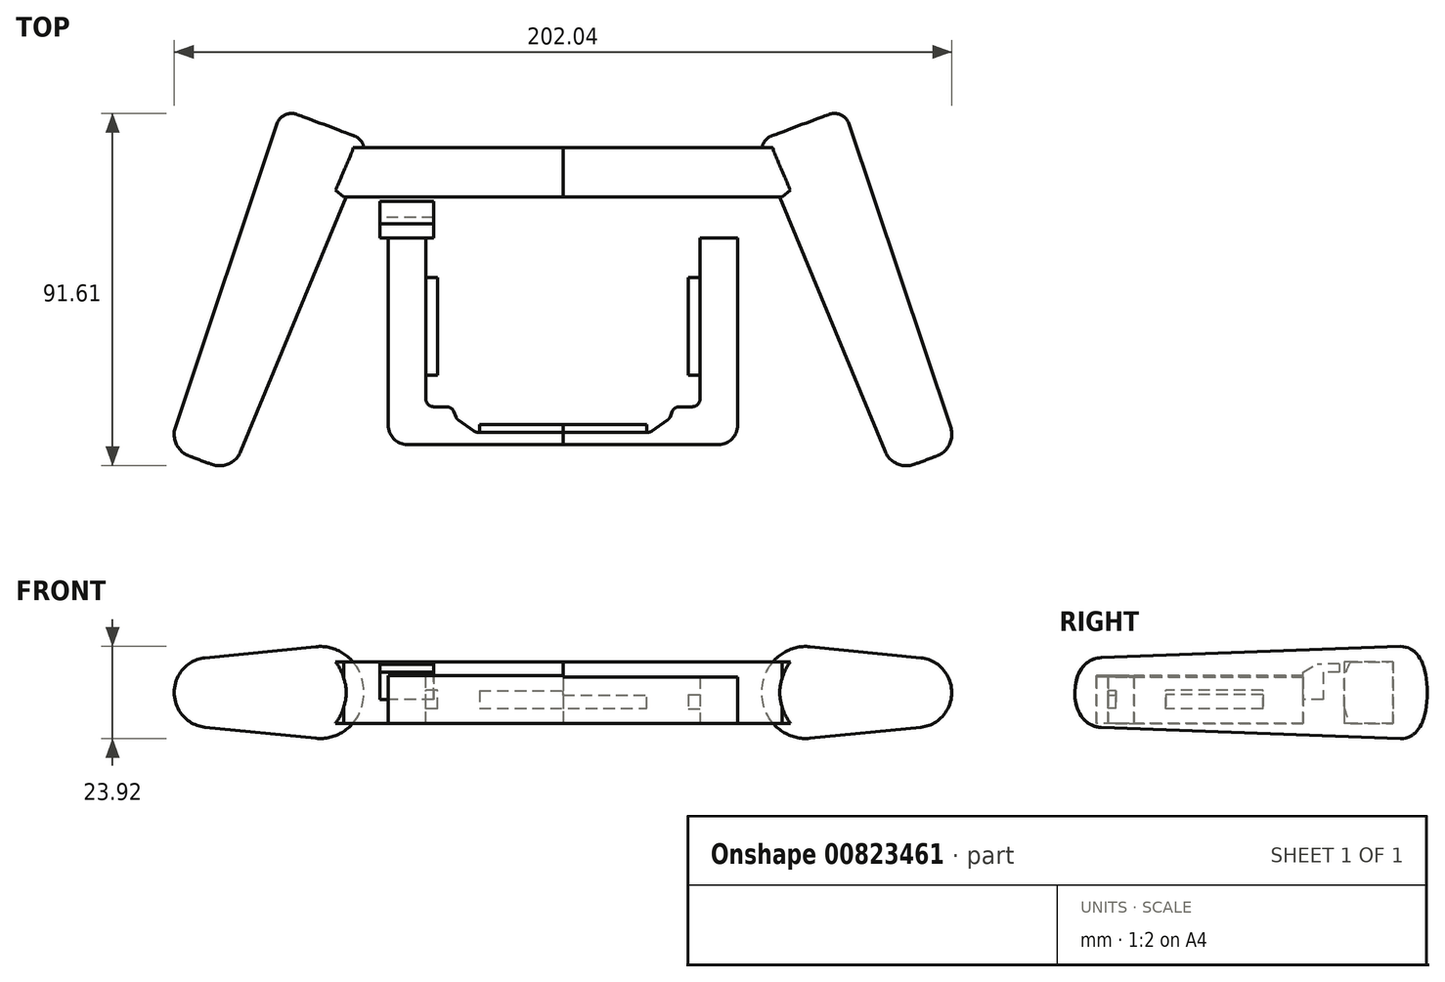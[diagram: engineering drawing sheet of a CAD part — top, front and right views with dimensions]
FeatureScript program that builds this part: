
annotation { "Feature Type Name" : "Feature", "Feature Type Description" : "" }
export const myFeature = defineFeature(function(context is Context, id is Id, definition is map)
    precondition{}
    {
        {
            var Q0;
            Q0=qCreatedBy(makeId("Top.planeOp"),FACE);
            var sketch = newSketch(context, id + "F0", { "sketchPlane" : qUnion([Q0])});
            skLineSegment(sketch, "E0", {"start": v(0, -25.8) * mm, "end": v(-45.43, -25.8) * mm});
            skLineSegment(sketch, "E1", {"start": v(-45.43, -25.8) * mm, "end": v(-45.43, 27.94) * mm});
            skLineSegment(sketch, "E2", {"start": v(-45.43, 27.94) * mm, "end": v(-35.62, 27.94) * mm});
            skLineSegment(sketch, "E3", {"start": v(-35.62, 27.94) * mm, "end": v(-35.62, -16) * mm});
            skLineSegment(sketch, "E4", {"start": v(-35.62, -16) * mm, "end": v(-28.9, -16) * mm});
            skLineSegment(sketch, "E5", {"start": v(0, -22.66) * mm, "end": v(0, -25.8) * mm});
            skLineSegment(sketch, "E6", {"start": v(-28.9, -16) * mm, "end": v(-27.58, -19.2) * mm});
            skLineSegment(sketch, "E7", {"start": v(-27.58, -19.2) * mm, "end": v(-22.63, -22.66) * mm});
            skLineSegment(sketch, "E8", {"start": v(-22.63, -22.66) * mm, "end": v(0, -22.66) * mm});
            skSolve(sketch);
        }
        {
            var Q0;
            Q0=makeQuery(id+"F0.imprint","IMPRINT",FACE,{"disambiguationData":[TD([[makeQuery(id+"F0.imprint","IMPRINT",EDGE,{"derivedFrom":sQuery(id+"F0.wireOp",EDGE,"E0")}),-1.0]])]});
            extrude(context, id + "F1", {"entities" : qUnion([Q0]), "depth" : 12 * mm, "offsetDistance" : 25 * mm});
        }
        {
            var Q0;
            Q0=makeQuery(id+"F1.opExtrude","SWEPT_FACE",FACE,{"disambiguationData":[OSD([sQuery(id+"F0.wireOp",EDGE,"E3")])]});
            var sketch = newSketch(context, id + "F2", { "sketchPlane" : qUnion([Q0])});
            skLineSegment(sketch, "E9.bottom", {"start": v(17.56, 7.38) * mm, "end": v(-7.78, 7.38) * mm});
            skLineSegment(sketch, "E9.top", {"start": v(17.56, 3.74) * mm, "end": v(-7.78, 3.74) * mm});
            skLineSegment(sketch, "E9.left", {"start": v(17.56, 7.38) * mm, "end": v(17.56, 3.74) * mm});
            skLineSegment(sketch, "E9.right", {"start": v(-7.78, 7.38) * mm, "end": v(-7.78, 3.74) * mm});
            skSolve(sketch);
        }
        {
            var Q0;
            Q0=makeQuery(id+"F2.imprint","IMPRINT",FACE,{"disambiguationData":[TD([[makeQuery(id+"F2.imprint","IMPRINT",EDGE,{"derivedFrom":sQuery(id+"F2.wireOp",EDGE,"E9.bottom")}),1.0]])]});
            extrude(context, id + "F3", {"entities" : qUnion([Q0]), "operationType" : NewBodyOperationType.ADD, "depth" : 3 * mm, "offsetDistance" : 25 * mm});
        }
        {
            var Q0;
            Q0=makeQuery(id+"F1.opExtrude","SWEPT_FACE",FACE,{"disambiguationData":[OSD([sQuery(id+"F0.wireOp",EDGE,"E8")])]});
            var sketch = newSketch(context, id + "F4", { "sketchPlane" : qUnion([Q0])});
            skLineSegment(sketch, "E10.bottom", {"start": v(21.7, 3.84) * mm, "end": v(0, 3.84) * mm});
            skLineSegment(sketch, "E10.top", {"start": v(21.7, 7.36) * mm, "end": v(0, 7.36) * mm});
            skLineSegment(sketch, "E10.left", {"start": v(21.7, 3.84) * mm, "end": v(21.7, 7.36) * mm});
            skLineSegment(sketch, "E10.right", {"start": v(0, 3.84) * mm, "end": v(0, 7.36) * mm});
            skSolve(sketch);
        }
        {
            var Q0;
            Q0=makeQuery(id+"F4.imprint","IMPRINT",FACE,{"disambiguationData":[TD([[makeQuery(id+"F4.imprint","IMPRINT",EDGE,{"derivedFrom":sQuery(id+"F4.wireOp",EDGE,"E10.bottom")}),-1.0]])]});
            extrude(context, id + "F5", {"entities" : qUnion([Q0]), "operationType" : NewBodyOperationType.ADD, "depth" : 2 * mm, "offsetDistance" : 25 * mm});
        }
        {
            var Q0;
            Q0=makeQuery(id+"F1.opExtrude","SWEPT_EDGE",EDGE,{"disambiguationData":[OSD([sQuery(id+"F0.wireOp",EDGE,"E0"),sQuery(id+"F0.wireOp",EDGE,"E1")])]});
            fillet(context, id + "F6", {"entities" : qUnion([Q0]), "radius" : 5 * mm, "tangentPropagation" : true, "allowEdgeOverflow" : false});
        }
        {
            var Q0;
            Q0=makeQuery(id+"F1.opExtrude","SWEPT_EDGE",EDGE,{"disambiguationData":[OSD([sQuery(id+"F0.wireOp",EDGE,"E4"),sQuery(id+"F0.wireOp",EDGE,"E6")])]});
            var Q1;
            Q1=makeQuery(id+"F1.opExtrude","SWEPT_EDGE",EDGE,{"disambiguationData":[OSD([sQuery(id+"F0.wireOp",EDGE,"E6"),sQuery(id+"F0.wireOp",EDGE,"E7")])]});
            var Q2;
            Q2=makeQuery(id+"F1.opExtrude","SWEPT_EDGE",EDGE,{"disambiguationData":[OSD([sQuery(id+"F0.wireOp",EDGE,"E7"),sQuery(id+"F0.wireOp",EDGE,"E8")])]});
            var Q3;
            Q3=makeQuery(id+"F1.opExtrude","SWEPT_EDGE",EDGE,{"disambiguationData":[OSD([sQuery(id+"F0.wireOp",EDGE,"E3"),sQuery(id+"F0.wireOp",EDGE,"E4")])]});
            fillet(context, id + "F7", {"entities" : qUnion([Q0, Q1, Q2, Q3]), "radius" : 2 * mm, "tangentPropagation" : true, "allowEdgeOverflow" : false});
        }
        {
            var Q0;
            Q0=makeQuery(id+"F1.opExtrude","SWEPT_FACE",FACE,{"disambiguationData":[OSD([sQuery(id+"F0.wireOp",EDGE,"E3")])]});
            var sketch = newSketch(context, id + "F8", { "sketchPlane" : qUnion([Q0])});
            skLineSegment(sketch, "E11", {"start": v(27.94, 6.18) * mm, "end": v(27.94, 13.28) * mm});
            skLineSegment(sketch, "E12", {"start": v(27.94, 13.28) * mm, "end": v(31.62, 15.36) * mm});
            skLineSegment(sketch, "E13", {"start": v(37.4, 15.43) * mm, "end": v(37.4, 13.28) * mm});
            skLineSegment(sketch, "E14", {"start": v(33.18, 12) * mm, "end": v(33.18, 6.18) * mm});
            skPoint(sketch, "E14.endSnap0", {"position": v(27.94, 6.18) * mm});
            skLineSegment(sketch, "E15", {"start": v(33.18, 6.18) * mm, "end": v(27.94, 6.18) * mm});
            skLineSegment(sketch, "E16", {"start": v(37.4, 15.43) * mm, "end": v(31.62, 15.36) * mm});
            skLineSegment(sketch, "E17", {"start": v(37.4, 13.28) * mm, "end": v(33.18, 13.23) * mm});
            skLineSegment(sketch, "E18", {"start": v(33.18, 13.23) * mm, "end": v(33.18, 12) * mm});
            skSolve(sketch);
        }
        {
            var Q0;
            {var subQ0=sQuery(id+"F8.wireOp",EDGE,"E12");Q0=makeQuery(id+"F8.imprint","IMPRINT",FACE,{"disambiguationData":[TD([[makeQuery(id+"F8.imprint","IMPRINT",EDGE,{"derivedFrom":subQ0}),-1.0]])]});}
            extrude(context, id + "F9", {"entities" : qUnion([Q0]), "operationType" : NewBodyOperationType.ADD, "depth" : 2 * mm, "offsetDistance" : 25 * mm, "hasSecondDirection" : true, "secondDirectionOppositeDirection" : true, "secondDirectionDepth" : 12 * mm});
        }
        {
            var Q0;
            Q0=makeQuery(id+"F1.opExtrude","SWEPT_BODY",BODY,{"disambiguationData":[OSD([sQuery(id+"F0.wireOp",EDGE,"E0"),sQuery(id+"F0.wireOp",EDGE,"E1"),sQuery(id+"F0.wireOp",EDGE,"E2"),sQuery(id+"F0.wireOp",EDGE,"E3"),sQuery(id+"F0.wireOp",EDGE,"E4"),sQuery(id+"F0.wireOp",EDGE,"E5"),sQuery(id+"F0.wireOp",EDGE,"E6"),sQuery(id+"F0.wireOp",EDGE,"E7"),sQuery(id+"F0.wireOp",EDGE,"E8")])]});
            var Q1;
            Q1=makeQuery(id+"F9.opExtrude","SWEPT_FACE",FACE,{"disambiguationData":[OSD([sQuery(id+"F8.wireOp",EDGE,"E15")])]});
            mirror(context, id + "F10", {"operationType" : NewBodyOperationType.ADD, "entities" : qUnion([Q0]), "mirrorPlane" : qUnion([Q1])});
        }
        {
            var Q0;
            Q0=makeQuery(id+"F1.opExtrude","SWEPT_BODY",BODY,{"disambiguationData":[OSD([sQuery(id+"F0.wireOp",EDGE,"E0"),sQuery(id+"F0.wireOp",EDGE,"E1"),sQuery(id+"F0.wireOp",EDGE,"E2"),sQuery(id+"F0.wireOp",EDGE,"E3"),sQuery(id+"F0.wireOp",EDGE,"E4"),sQuery(id+"F0.wireOp",EDGE,"E5"),sQuery(id+"F0.wireOp",EDGE,"E6"),sQuery(id+"F0.wireOp",EDGE,"E7"),sQuery(id+"F0.wireOp",EDGE,"E8")])]});
            var Q1;
            Q1=qCreatedBy(makeId("Right.planeOp"),FACE);
            mirror(context, id + "F11", {"operationType" : NewBodyOperationType.ADD, "entities" : qUnion([Q0]), "mirrorPlane" : qUnion([Q1])});
        }
        {
            var Q0;
            Q0=qCreatedBy(makeId("Top.planeOp"),FACE);
            var sketch = newSketch(context, id + "F12", { "sketchPlane" : qUnion([Q0])});
            skLineSegment(sketch, "E19", {"start": v(0, 38.6) * mm, "end": v(-56.94, 38.6) * mm});
            skLineSegment(sketch, "E20", {"start": v(-54.66, 51.4) * mm, "end": v(0, 51.4) * mm});
            skLineSegment(sketch, "E21", {"start": v(0, 51.4) * mm, "end": v(0, 38.6) * mm});
            skLineSegment(sketch, "E22", {"start": v(-54.66, 51.4) * mm, "end": v(-70.84, 57.44) * mm});
            skLineSegment(sketch, "E23", {"start": v(-73.1, 51.4) * mm, "end": v(-70.84, 57.44) * mm});
            skLineSegment(sketch, "E24", {"start": v(-73.1, 51.4) * mm, "end": v(-56.94, 38.6) * mm});
            skSolve(sketch);
        }
        {
            var Q0;
            Q0=makeQuery(id+"F12.imprint","IMPRINT",FACE,{"disambiguationData":[TD([[makeQuery(id+"F12.imprint","IMPRINT",EDGE,{"derivedFrom":sQuery(id+"F12.wireOp",EDGE,"E19")}),-1.0]])]});
            extrude(context, id + "F13", {"entities" : qUnion([Q0]), "depth" : 16 * mm, "offsetDistance" : 25 * mm});
        }
        {
            var Q0;
            Q0=makeQuery(id+"F13.opExtrude","SWEPT_FACE",FACE,{"disambiguationData":[OSD([sQuery(id+"F12.wireOp",EDGE,"E22")])]});
            var sketch = newSketch(context, id + "F14", { "sketchPlane" : qUnion([Q0])});
            skCircle(sketch, "E25", {"center": v(77.83, 8) * mm, "radius": 12 * mm});
            skPoint(sketch, "E25.centerSnap0", {"position": v(86.47, 8) * mm});
            skPoint(sketch, "E25.centerSnap1", {"position": v(77.83, 0) * mm});
            skSolve(sketch);
        }
        {
            var Q0;
            Q0 = qSketchRegion(id + "F14", true);
            extrude(context, id + "F15", {"entities" : qUnion([Q0]), "operationType" : NewBodyOperationType.ADD, "oppositeDirection" : true, "depth" : 90 * mm, "offsetDistance" : 25 * mm, "hasDraft" : true, "draftAngle" : 2 * degree, "draftPullDirection" : true, "hasSecondDirection" : true, "secondDirectionOppositeDirection" : false, "secondDirectionDepth" : 3 * mm, "hasSecondDirectionDraft" : true, "secondDirectionDraftAngle" : 2 * degree});
        }
        {
            var Q0;
            Q0=makeQuery(id+"F15.opExtrude","CAP_EDGE",EDGE,{"disambiguationData":[OSD([sQuery(id+"F14.wireOp",EDGE,"E25")])],"isStart":false});
            fillet(context, id + "F16", {"entities" : qUnion([Q0]), "radius" : 6 * mm, "tangentPropagation" : true, "allowEdgeOverflow" : false});
        }
        {
            var Q0;
            Q0=makeQuery(id+"F15.opExtrude","CAP_EDGE",EDGE,{"disambiguationData":[OSD([sQuery(id+"F14.wireOp",EDGE,"E25")])],"isStart":true});
            fillet(context, id + "F17", {"entities" : qUnion([Q0]), "radius" : 4 * mm, "tangentPropagation" : true, "allowEdgeOverflow" : false});
        }
        {
            var Q0;
            Q0=makeQuery(id+"F13.opExtrude","SWEPT_BODY",BODY,{"disambiguationData":[OSD([sQuery(id+"F12.wireOp",EDGE,"E19"),sQuery(id+"F12.wireOp",EDGE,"KtcvXK5F-ZELN-fU7s-A6mI-Q6N2E6gRVcH1"),sQuery(id+"F12.wireOp",EDGE,"Qn31sEN5-pv0t-c1kq-lJQx-FveNBIpDBRZT"),sQuery(id+"F12.wireOp",EDGE,"fs8QF1FP-RA4e-XUg5-KfBe-J54YNQtL5PfG"),sQuery(id+"F12.wireOp",EDGE,"E20"),sQuery(id+"F12.wireOp",EDGE,"E21")])]});
            var Q1;
            Q1=qCreatedBy(makeId("Right.planeOp"),FACE);
            mirror(context, id + "F18", {"operationType" : NewBodyOperationType.ADD, "entities" : qUnion([Q0]), "mirrorPlane" : qUnion([Q1])});
        }
    });
